# Revit family: Verbindungsstück 45
name_source: partatom
category: HLS-Bauteile
revit_build: Autodesk Revit 2017 (Build: 20190507_1515(x64)
units: mm (PartAtom-declared; Revit-internal decimal feet)

## family parameters
Arbeitsebenenbasiert = Ja
Beim Laden mit Abzugskörper schneiden = Nein
Bemaßung runder Anschluss = Durchmesser verwenden
Gemeinsam genutzt = Ja
Immer vertikal = Nein
Raumberechnungspunkt = Nein
Teiletyp = Normal

## types (2) — shared parameters
Breite = 49 mm
Fabrikat = MEFA
Firma = MEFA Befestigungs- und Montagesysteme GmbH
Gewicht = 1.47 kg
Gewicht pro Bauteil = 1.47 kg
Höhe = 42.7 mm
Kurztext2 = 350x48,5x42,7 mm Lochd. 13x50 mm
Langloch = 13x50 mm
Material = Stahl
Profil = C-Profil
Profiltyp = 45
Vorgabe-Ansicht = 1219 mm

## per-type parameters (varying)
| type | Artikelnummer | EAN | Kurztext1 |
| Verbindungsstück 45 | 08162002 | 4250928456779 | Verbindungsstück C-Profil 45 |
| Verbindungsstück 45 zn | 08162002/zn | 4250928457417 | Verbindungsstück C-Profil 45 ZnNi |
